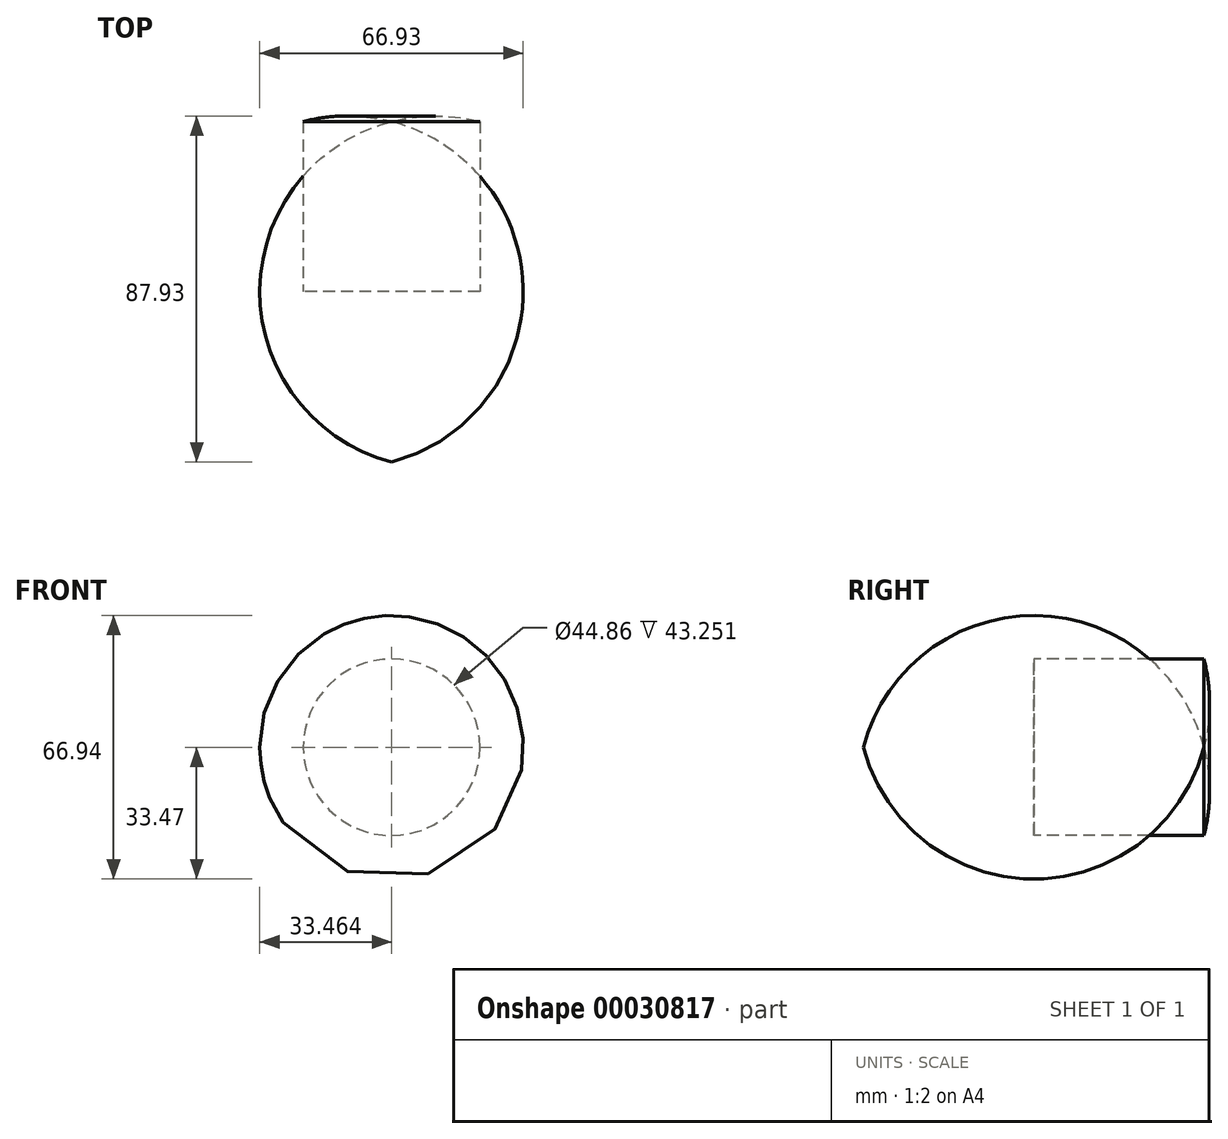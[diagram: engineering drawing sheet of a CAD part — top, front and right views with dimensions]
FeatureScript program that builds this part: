
annotation { "Feature Type Name" : "Feature", "Feature Type Description" : "" }
export const myFeature = defineFeature(function(context is Context, id is Id, definition is map)
    precondition{}
    {
        {
            var Q0;
            Q0=qCreatedBy(makeId("Top.planeOp"),FACE);
            var sketch = newSketch(context, id + "F0", { "sketchPlane" : qUnion([Q0])});
            skArc(sketch, "E0", {"start": v(11.21, 43.25) * mm, "mid": v(0, 44.68) * mm, "end": v(-11.21, 43.25) * mm});
            skLineSegment(sketch, "E1", {"start": v(0, 0) * mm, "end": v(11.21, 0) * mm});
            skLineSegment(sketch, "E2", {"start": v(11.21, 0) * mm, "end": v(11.21, 43.25) * mm});
            skLineSegment(sketch, "E3", {"start": v(11.21, 43.25) * mm, "end": v(11.21, 0) * mm});
            skLineSegment(sketch, "E4", {"start": v(-11.21, 0) * mm, "end": v(-11.21, 43.25) * mm});
            skLineSegment(sketch, "E5", {"start": v(0, 0) * mm, "end": v(-11.21, 0) * mm});
            skLineSegment(sketch, "E6", {"start": v(-11.21, 0) * mm, "end": v(11.21, 0) * mm});
            skLineSegment(sketch, "E7", {"start": v(11.21, 0) * mm, "end": v(-11.21, 0) * mm});
            skSolve(sketch);
        }
        {
            var Q0;
            Q0=makeQuery(id+"F0.imprint","IMPRINT",FACE,{"disambiguationData":[TD([[makeQuery(id+"F0.imprint","IMPRINT",EDGE,{"derivedFrom":sQuery(id+"F0.wireOp",EDGE,"E0")}),1.0]])]});
            var Q1;
            Q1=sQuery(id+"F0.wireOp",EDGE,"E2");
            revolve(context, id + "F1", {"entities" : qUnion([Q0]), "axis" : qUnion([Q1]), "revolveType" : RevolveType.FULL});
        }
    });
